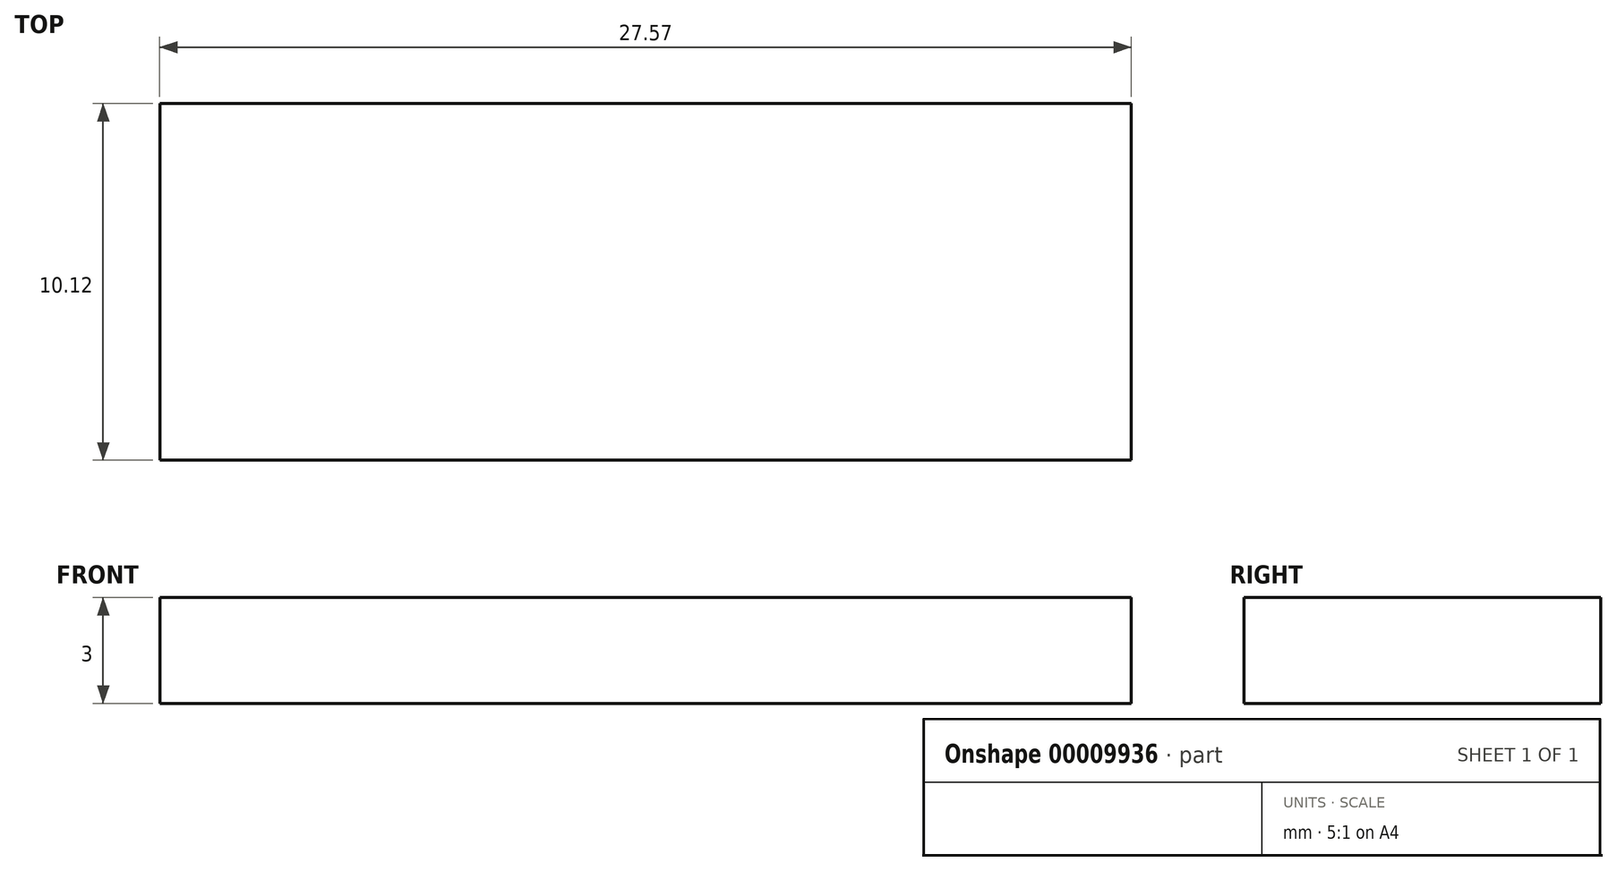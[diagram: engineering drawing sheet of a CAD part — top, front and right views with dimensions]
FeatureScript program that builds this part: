
annotation { "Feature Type Name" : "Feature", "Feature Type Description" : "" }
export const myFeature = defineFeature(function(context is Context, id is Id, definition is map)
    precondition{}
    {
        {
            var Q0;
            Q0=qCreatedBy(makeId("Top.planeOp"),FACE);
            var sketch = newSketch(context, id + "F0", { "sketchPlane" : qUnion([Q0])});
            skLineSegment(sketch, "E0.bottom", {"start": v(-11.89, 4.08) * mm, "end": v(15.68, 4.08) * mm});
            skLineSegment(sketch, "E0.top", {"start": v(-11.89, -6.04) * mm, "end": v(15.68, -6.04) * mm});
            skLineSegment(sketch, "E0.left", {"start": v(-11.89, 4.08) * mm, "end": v(-11.89, -6.04) * mm});
            skLineSegment(sketch, "E0.right", {"start": v(15.68, 4.08) * mm, "end": v(15.68, -6.04) * mm});
            skSolve(sketch);
        }
        {
            var Q0;
            Q0 = qSketchRegion(id + "F0", true);
            extrude(context, id + "F1", {"entities" : qUnion([Q0]), "depth" : 3 * mm});
        }
    });
